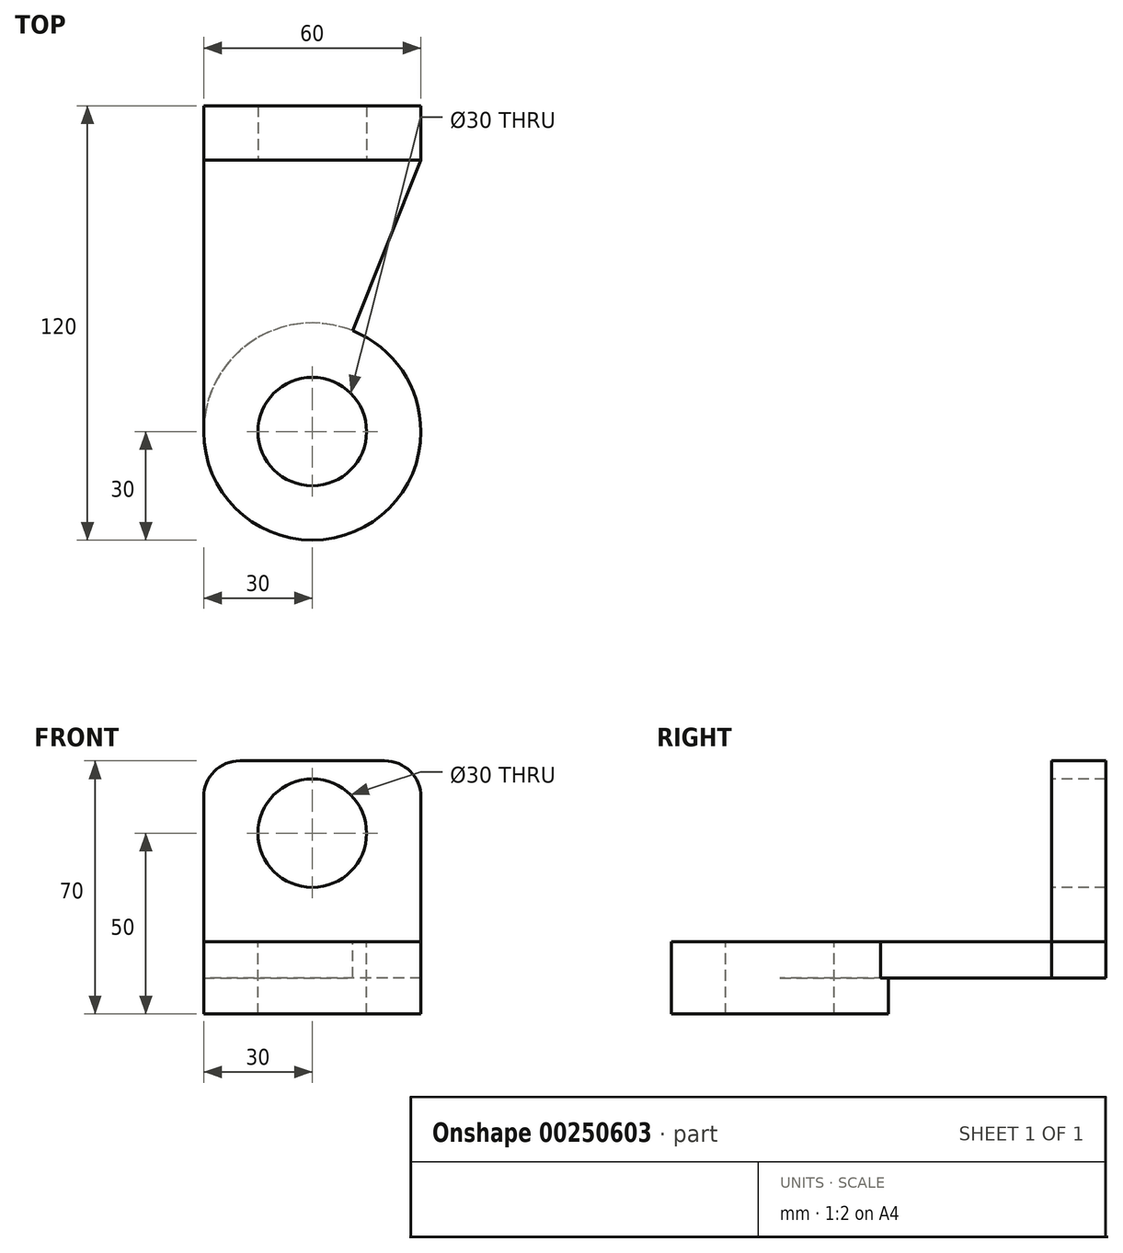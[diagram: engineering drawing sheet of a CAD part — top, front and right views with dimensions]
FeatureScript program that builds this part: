
annotation { "Feature Type Name" : "Feature", "Feature Type Description" : "" }
export const myFeature = defineFeature(function(context is Context, id is Id, definition is map)
    precondition{}
    {
        {
            var Q0;
            Q0=qCreatedBy(makeId("Front.planeOp"),FACE);
            var sketch = newSketch(context, id + "F0", { "sketchPlane" : qUnion([Q0])});
            skLineSegment(sketch, "E0.bottom", {"start": v(20, 25) * mm, "end": v(-20, 25) * mm});
            skLineSegment(sketch, "E0.top", {"start": v(30, -25) * mm, "end": v(-30, -25) * mm});
            skLineSegment(sketch, "E0.left", {"start": v(30, 15) * mm, "end": v(30, -25) * mm});
            skLineSegment(sketch, "E0.right", {"start": v(-30, 15) * mm, "end": v(-30, -25) * mm});
            skPoint(sketch, "E0.middle", {"position": v(0, 0) * mm});
            skPoint(sketch, "E1.visualSharp", {"position": v(-30, 25) * mm});
            skArc(sketch, "E1.filletArc", {"start": v(-20, 25) * mm, "mid": v(-27.07, 22.07) * mm, "end": v(-30, 15) * mm});
            skPoint(sketch, "E2.visualSharp", {"position": v(30, 25) * mm});
            skArc(sketch, "E2.filletArc", {"start": v(30, 15) * mm, "mid": v(27.07, 22.07) * mm, "end": v(20, 25) * mm});
            skSolve(sketch);
        }
        {
            var Q0;
            Q0=makeQuery(id+"F0.imprint","IMPRINT",FACE,{"disambiguationData":[TD([[makeQuery(id+"F0.imprint","IMPRINT",EDGE,{"derivedFrom":sQuery(id+"F0.wireOp",EDGE,"E0.bottom")}),1.0]])]});
            extrude(context, id + "F1", {"entities" : qUnion([Q0]), "depth" : 15 * mm});
        }
        {
            var Q0;
            Q0=makeQuery(id+"F1.opExtrude","CAP_FACE",FACE,{"disambiguationData":[OSD([sQuery(id+"F0.wireOp",EDGE,"E0.bottom"),sQuery(id+"F0.wireOp",EDGE,"E0.top"),sQuery(id+"F0.wireOp",EDGE,"E0.left"),sQuery(id+"F0.wireOp",EDGE,"E0.right"),sQuery(id+"F0.wireOp",EDGE,"E1.filletArc"),sQuery(id+"F0.wireOp",EDGE,"E2.filletArc")])],"isStart":false});
            var sketch = newSketch(context, id + "F2", { "sketchPlane" : qUnion([Q0])});
            skLineSegment(sketch, "E3", {"start": v(0, -25) * mm, "end": v(0, 5) * mm, "construction": true});
            skPoint(sketch, "E3.endSnap0", {"position": v(0, -25) * mm});
            skCircle(sketch, "E4", {"center": v(0, 5) * mm, "radius": 15 * mm});
            skSolve(sketch);
        }
        {
            var Q0;
            Q0=makeQuery(id+"F2.imprint","IMPRINT",FACE,{"disambiguationData":[TD([[makeQuery(id+"F2.imprint","IMPRINT",EDGE,{"derivedFrom":sQuery(id+"F2.wireOp",EDGE,"E4")}),1.0]])]});
            extrude(context, id + "F3", {"entities" : qUnion([Q0]), "oppositeDirection" : true, "depth" : 25 * mm, "hasSecondDirection" : true, "secondDirectionOppositeDirection" : false, "secondDirectionDepth" : 25 * mm});
        }
        {
            var Q0;
            Q0=makeQuery(id+"F3.opExtrude","SWEPT_BODY",BODY,{"disambiguationData":[OSD([sQuery(id+"F2.wireOp",EDGE,"E4")])]});
            var Q1;
            Q1=makeQuery(id+"F1.opExtrude","SWEPT_BODY",BODY,{"disambiguationData":[OSD([sQuery(id+"F0.wireOp",EDGE,"E0.bottom"),sQuery(id+"F0.wireOp",EDGE,"E0.top"),sQuery(id+"F0.wireOp",EDGE,"E0.left"),sQuery(id+"F0.wireOp",EDGE,"E0.right"),sQuery(id+"F0.wireOp",EDGE,"E1.filletArc"),sQuery(id+"F0.wireOp",EDGE,"E2.filletArc")])]});
            booleanBodies(context, id + "F4", {"operationType" : BooleanOperationType.SUBTRACTION, "tools" : qUnion([Q0]), "targets" : qUnion([Q1])});
        }
        {
            var Q0;
            Q0=makeQuery(id+"F1.opExtrude","SWEPT_FACE",FACE,{"disambiguationData":[OSD([sQuery(id+"F0.wireOp",EDGE,"E0.top")])]});
            var sketch = newSketch(context, id + "F5", { "sketchPlane" : qUnion([Q0])});
            skLineSegment(sketch, "E5", {"start": v(-30, 15) * mm, "end": v(-30, 90) * mm});
            skLineSegment(sketch, "E6", {"start": v(-30, 90) * mm, "end": v(0, 90) * mm});
            skLineSegment(sketch, "E7", {"start": v(30, 15) * mm, "end": v(0, 90) * mm});
            skSolve(sketch);
        }
        {
            var Q0;
            Q0=makeQuery(id+"F5.imprint","IMPRINT",FACE,{"disambiguationData":[TD([[makeQuery(id+"F5.imprint","IMPRINT",EDGE,{"derivedFrom":sQuery(id+"F5.wireOp",EDGE,"E5")}),-1.0]])]});
            extrude(context, id + "F6", {"entities" : qUnion([Q0]), "depth" : 10 * mm});
        }
        {
            var Q0;
            Q0=makeQuery(id+"F6.opExtrude","SWEPT_FACE",FACE,{"disambiguationData":[OSD([sQuery(id+"F0.wireOp",EDGE,"E0.top")])]});
            extrude(context, id + "F7", {"entities" : qUnion([Q0]), "depth" : 15 * mm});
        }
        {
            var Q0;
            Q0=makeQuery(id+"F6.opExtrude","CAP_FACE",FACE,{"disambiguationData":[OSD([sQuery(id+"F0.wireOp",EDGE,"E0.top"),sQuery(id+"F5.wireOp",EDGE,"E5"),sQuery(id+"F5.wireOp",EDGE,"E6"),sQuery(id+"F5.wireOp",EDGE,"E7")])],"isStart":true});
            var sketch = newSketch(context, id + "F8", { "sketchPlane" : qUnion([Q0])});
            skCircle(sketch, "E8", {"center": v(0, -90) * mm, "radius": 30 * mm});
            skCircle(sketch, "E9", {"center": v(0, -90) * mm, "radius": 15 * mm});
            skSolve(sketch);
        }
        {
            var Q0;
            {var subQ0=sQuery(id+"F8.wireOp",EDGE,"E9");var subQ1=makeQuery(id+"F6.opExtrude","CAP_EDGE",EDGE,{"disambiguationData":[OSD([sQuery(id+"F5.wireOp",EDGE,"E6")])],"isStart":true});var subQ2=makeQuery(id+"F8.imprint","INTERSECT",VERTEX,{"derivedFrom":[subQ1,subQ0]});Q0=makeQuery(id+"F8.imprint","IMPRINT",FACE,{"disambiguationData":[TD([[makeQuery(id+"F8.imprint","IMPRINT",EDGE,{"disambiguationData":[TD([[subQ2,1.0]])],"derivedFrom":subQ0}),1.0]])]});}
            extrude(context, id + "F9", {"entities" : qUnion([Q0]), "operationType" : NewBodyOperationType.REMOVE, "oppositeDirection" : true, "depth" : 10 * mm});
        }
        {
            var Q0;
            {var subQ1=makeQuery(id+"F6.opExtrude","CAP_EDGE",EDGE,{"disambiguationData":[OSD([sQuery(id+"F5.wireOp",EDGE,"E6")])],"isStart":true});var subQ5=sQuery(id+"F8.wireOp",EDGE,"E9");var subQ6=makeQuery(id+"F8.imprint","INTERSECT",VERTEX,{"derivedFrom":[subQ1,subQ5]});Q0=makeQuery(id+"F8.imprint","IMPRINT",FACE,{"disambiguationData":[TD([[makeQuery(id+"F8.imprint","IMPRINT",EDGE,{"disambiguationData":[TD([[subQ6,-1.0]])],"derivedFrom":subQ5}),-1.0]])]});}
            extrude(context, id + "F10", {"entities" : qUnion([Q0]), "operationType" : NewBodyOperationType.ADD, "oppositeDirection" : true, "depth" : 20 * mm});
        }
        {
            var Q0;
            {var subQ1=makeQuery(id+"F6.opExtrude","CAP_EDGE",EDGE,{"disambiguationData":[OSD([sQuery(id+"F5.wireOp",EDGE,"E6")])],"isStart":true});var subQ5=sQuery(id+"F8.wireOp",EDGE,"E9");var subQ7=makeQuery(id+"F8.imprint","INTERSECT",VERTEX,{"derivedFrom":[subQ1,subQ5]});Q0=makeQuery(id+"F8.imprint","IMPRINT",FACE,{"disambiguationData":[TD([[makeQuery(id+"F8.imprint","IMPRINT",EDGE,{"disambiguationData":[TD([[subQ7,1.0]])],"derivedFrom":subQ5}),-1.0]])]});}
            extrude(context, id + "F11", {"entities" : qUnion([Q0]), "operationType" : NewBodyOperationType.ADD, "oppositeDirection" : true, "depth" : 20 * mm});
        }
    });
